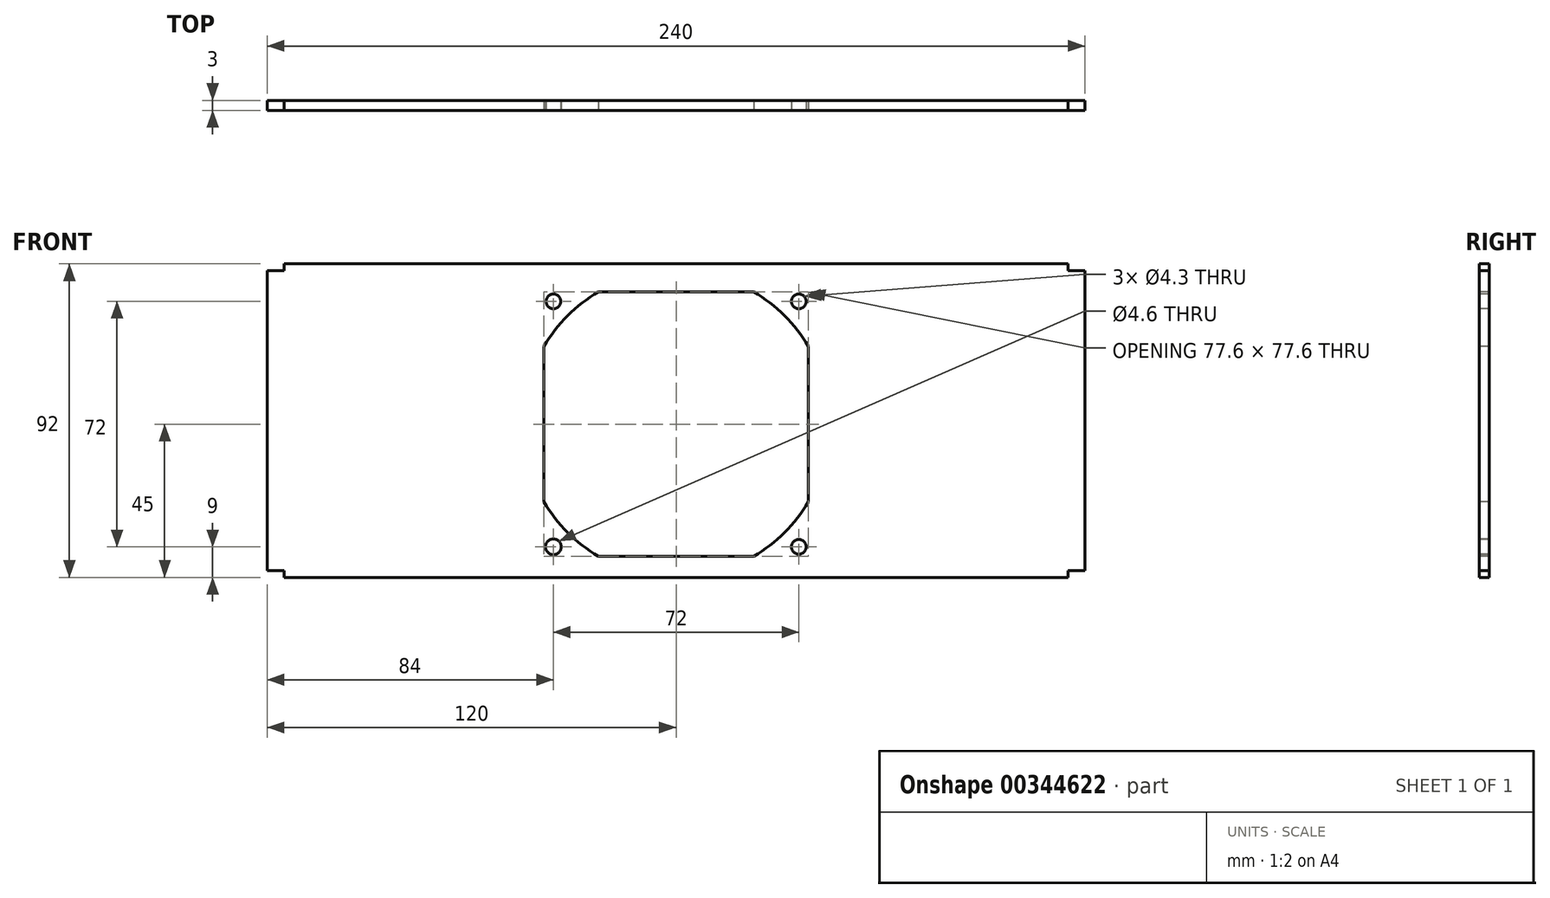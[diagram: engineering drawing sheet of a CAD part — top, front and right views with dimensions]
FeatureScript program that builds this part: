
annotation { "Feature Type Name" : "Feature", "Feature Type Description" : "" }
export const myFeature = defineFeature(function(context is Context, id is Id, definition is map)
    precondition{}
    {
        {
            var Q0;
            Q0=qCreatedBy(makeId("Front.planeOp"),FACE);
            var sketch = newSketch(context, id + "F0", { "sketchPlane" : qUnion([Q0])});
            skLineSegment(sketch, "E0.bottom", {"start": v(120, -47) * mm, "end": v(-120, -47) * mm});
            skLineSegment(sketch, "E0.top", {"start": v(120, 47) * mm, "end": v(-120, 47) * mm});
            skLineSegment(sketch, "E0.left", {"start": v(120, -47) * mm, "end": v(120, 47) * mm});
            skLineSegment(sketch, "E0.right", {"start": v(-120, -47) * mm, "end": v(-120, 47) * mm});
            skPoint(sketch, "E0.middle", {"position": v(0, 0) * mm});
            skSolve(sketch);
        }
        {
            var Q0;
            Q0=qSketchRegion(id+"F0",true);
            extrude(context, id + "F1", {"entities" : qUnion([Q0]), "depth" : 3 * mm});
        }
        {
            var Q0;
            Q0=makeQuery(id+"F1.opExtrude","CAP_FACE",FACE,{"disambiguationData":[OSD([sQuery(id+"F0.wireOp",EDGE,"E0.bottom"),sQuery(id+"F0.wireOp",EDGE,"E0.top"),sQuery(id+"F0.wireOp",EDGE,"E0.left"),sQuery(id+"F0.wireOp",EDGE,"E0.right")])],"isStart":false});
            var sketch = newSketch(context, id + "F2", { "sketchPlane" : qUnion([Q0])});
            skLineSegment(sketch, "E1.bottom", {"start": v(-120, 47) * mm, "end": v(-115, 47) * mm});
            skLineSegment(sketch, "E1.top", {"start": v(-120, 45) * mm, "end": v(-115, 45) * mm});
            skLineSegment(sketch, "E1.left", {"start": v(-120, 47) * mm, "end": v(-120, 45) * mm});
            skLineSegment(sketch, "E1.right", {"start": v(-115, 47) * mm, "end": v(-115, 45) * mm});
            skLineSegment(sketch, "E2.bottom", {"start": v(-120, -47) * mm, "end": v(-115, -47) * mm});
            skLineSegment(sketch, "E2.top", {"start": v(-120, -43) * mm, "end": v(-115, -43) * mm});
            skLineSegment(sketch, "E2.left", {"start": v(-120, -47) * mm, "end": v(-120, -43) * mm});
            skLineSegment(sketch, "E2.right", {"start": v(-115, -47) * mm, "end": v(-115, -43) * mm});
            skLineSegment(sketch, "E3.bottom", {"start": v(120, -47) * mm, "end": v(115, -47) * mm});
            skLineSegment(sketch, "E3.top", {"start": v(120, -43) * mm, "end": v(115, -43) * mm});
            skLineSegment(sketch, "E3.left", {"start": v(120, -47) * mm, "end": v(120, -43) * mm});
            skLineSegment(sketch, "E3.right", {"start": v(115, -47) * mm, "end": v(115, -43) * mm});
            skLineSegment(sketch, "E4.bottom", {"start": v(120, 47) * mm, "end": v(115, 47) * mm});
            skLineSegment(sketch, "E4.top", {"start": v(120, 45) * mm, "end": v(115, 45) * mm});
            skLineSegment(sketch, "E4.left", {"start": v(120, 47) * mm, "end": v(120, 45) * mm});
            skLineSegment(sketch, "E4.right", {"start": v(115, 47) * mm, "end": v(115, 45) * mm});
            skLineSegment(sketch, "E5.bottom", {"start": v(115, -47) * mm, "end": v(-115, -47) * mm});
            skLineSegment(sketch, "E5.top", {"start": v(115, -45) * mm, "end": v(-115, -45) * mm});
            skLineSegment(sketch, "E5.left", {"start": v(115, -47) * mm, "end": v(115, -45) * mm});
            skLineSegment(sketch, "E5.right", {"start": v(-115, -47) * mm, "end": v(-115, -45) * mm});
            skSolve(sketch);
        }
        {
            var Q0;
            Q0=qSketchRegion(id+"F2",true);
            extrude(context, id + "F3", {"entities" : qUnion([Q0]), "operationType" : NewBodyOperationType.REMOVE, "oppositeDirection" : true, "depth" : 25 * mm});
        }
        {
            var Q0;
            Q0=makeQuery(id+"F1.opExtrude","CAP_FACE",FACE,{"disambiguationData":[OSD([sQuery(id+"F0.wireOp",EDGE,"E0.bottom"),sQuery(id+"F0.wireOp",EDGE,"E0.top"),sQuery(id+"F0.wireOp",EDGE,"E0.left"),sQuery(id+"F0.wireOp",EDGE,"E0.right")])],"isStart":false});
            var sketch = newSketch(context, id + "F4", { "sketchPlane" : qUnion([Q0])});
            skLineSegment(sketch, "E6.bottom", {"start": v(40, -40) * mm, "end": v(-40, -40) * mm});
            skLineSegment(sketch, "E6.top", {"start": v(40, 40) * mm, "end": v(-40, 40) * mm});
            skLineSegment(sketch, "E6.left", {"start": v(40, -40) * mm, "end": v(40, 40) * mm});
            skLineSegment(sketch, "E6.right", {"start": v(-40, -40) * mm, "end": v(-40, 40) * mm});
            skPoint(sketch, "E6.middle", {"position": v(0, 0) * mm});
            skLineSegment(sketch, "E7.bottom", {"start": v(36, -36) * mm, "end": v(27, -36) * mm});
            skLineSegment(sketch, "E7.top", {"start": v(36, 36) * mm, "end": v(27, 36) * mm});
            skLineSegment(sketch, "E7.left", {"start": v(36, -36) * mm, "end": v(36, -27) * mm});
            skLineSegment(sketch, "E7.right", {"start": v(-36, -36) * mm, "end": v(-36, -27) * mm});
            skCircle(sketch, "E8", {"center": v(-36, 36) * mm, "radius": 2.15 * mm});
            skCircle(sketch, "E9", {"center": v(36, 36) * mm, "radius": 2.15 * mm});
            skCircle(sketch, "E10", {"center": v(36, -36) * mm, "radius": 2.15 * mm});
            skCircle(sketch, "E11", {"center": v(-36, -36) * mm, "radius": 2.3 * mm});
            skArc(sketch, "E12", {"start": v(22.8, -38.8) * mm, "mid": v(31.82, -31.82) * mm, "end": v(38.8, -22.8) * mm});
            skArc(sketch, "E13.trimOffspring", {"start": v(-38.8, -22.8) * mm, "mid": v(-31.82, -31.82) * mm, "end": v(-22.8, -38.8) * mm});
            skArc(sketch, "E14.trimOffspring", {"start": v(-22.8, 38.8) * mm, "mid": v(-31.82, 31.82) * mm, "end": v(-38.8, 22.8) * mm});
            skArc(sketch, "E15.trimOffspring", {"start": v(38.8, 22.8) * mm, "mid": v(31.82, 31.82) * mm, "end": v(22.8, 38.8) * mm});
            skLineSegment(sketch, "E16.bottom", {"start": v(38.8, -38.8) * mm, "end": v(-38.8, -38.8) * mm});
            skLineSegment(sketch, "E16.top", {"start": v(38.8, 38.8) * mm, "end": v(-38.8, 38.8) * mm});
            skLineSegment(sketch, "E16.left", {"start": v(38.8, -38.8) * mm, "end": v(38.8, 38.8) * mm});
            skLineSegment(sketch, "E16.right", {"start": v(-38.8, -38.8) * mm, "end": v(-38.8, 38.8) * mm});
            skLineSegment(sketch, "E17.trimOffspring", {"start": v(-36, 27) * mm, "end": v(-36, 36) * mm});
            skLineSegment(sketch, "E18.trimOffspring", {"start": v(36, 27) * mm, "end": v(36, 36) * mm});
            skLineSegment(sketch, "E19.trimOffspring", {"start": v(-27, 36) * mm, "end": v(-36, 36) * mm});
            skLineSegment(sketch, "E20.trimOffspring", {"start": v(-27, -36) * mm, "end": v(-36, -36) * mm});
            skSolve(sketch);
        }
        {
            var Q0;
            {var subQ0=sQuery(id+"F4.wireOp",EDGE,"E17.trimOffspring");var subQ1=sQuery(id+"F4.wireOp",EDGE,"E8");var subQ2=makeQuery(id+"F4.imprint","INTERSECT",VERTEX,{"derivedFrom":[subQ1,subQ0]});Q0=makeQuery(id+"F4.imprint","IMPRINT",FACE,{"disambiguationData":[TD([[makeQuery(id+"F4.imprint","IMPRINT",EDGE,{"disambiguationData":[TD([[subQ2,1.0]])],"derivedFrom":subQ1}),1.0]])]});}
            var Q1;
            {var subQ0=sQuery(id+"F4.wireOp",EDGE,"E17.trimOffspring");var subQ1=sQuery(id+"F4.wireOp",EDGE,"E8");var subQ2=makeQuery(id+"F4.imprint","INTERSECT",VERTEX,{"derivedFrom":[subQ1,subQ0]});Q1=makeQuery(id+"F4.imprint","IMPRINT",FACE,{"disambiguationData":[TD([[makeQuery(id+"F4.imprint","IMPRINT",EDGE,{"disambiguationData":[TD([[subQ2,-1.0]])],"derivedFrom":subQ1}),1.0]])]});}
            var Q2;
            {var subQ0=sQuery(id+"F4.wireOp",EDGE,"E18.trimOffspring");var subQ1=sQuery(id+"F4.wireOp",EDGE,"E7.top");var subQ2=makeQuery(id+"F4.imprint","INTERSECT",VERTEX,{"derivedFrom":[subQ1,subQ0]});Q2=makeQuery(id+"F4.imprint","IMPRINT",FACE,{"disambiguationData":[TD([[makeQuery(id+"F4.imprint","IMPRINT",EDGE,{"disambiguationData":[TD([[subQ2,-1.0]])],"derivedFrom":subQ1}),-1.0]])]});}
            var Q3;
            {var subQ0=sQuery(id+"F4.wireOp",EDGE,"E18.trimOffspring");var subQ1=sQuery(id+"F4.wireOp",EDGE,"E7.top");var subQ2=makeQuery(id+"F4.imprint","INTERSECT",VERTEX,{"derivedFrom":[subQ1,subQ0]});Q3=makeQuery(id+"F4.imprint","IMPRINT",FACE,{"disambiguationData":[TD([[makeQuery(id+"F4.imprint","IMPRINT",EDGE,{"disambiguationData":[TD([[subQ2,-1.0]])],"derivedFrom":subQ1}),1.0]])]});}
            var Q4;
            {var subQ0=sQuery(id+"F4.wireOp",EDGE,"E7.left");var subQ1=sQuery(id+"F4.wireOp",EDGE,"E7.bottom");var subQ2=makeQuery(id+"F4.imprint","INTERSECT",VERTEX,{"derivedFrom":[subQ1,subQ0]});Q4=makeQuery(id+"F4.imprint","IMPRINT",FACE,{"disambiguationData":[TD([[makeQuery(id+"F4.imprint","IMPRINT",EDGE,{"disambiguationData":[TD([[subQ2,-1.0]])],"derivedFrom":subQ1}),1.0]])]});}
            var Q5;
            {var subQ0=sQuery(id+"F4.wireOp",EDGE,"E7.left");var subQ1=sQuery(id+"F4.wireOp",EDGE,"E7.bottom");var subQ2=makeQuery(id+"F4.imprint","INTERSECT",VERTEX,{"derivedFrom":[subQ1,subQ0]});Q5=makeQuery(id+"F4.imprint","IMPRINT",FACE,{"disambiguationData":[TD([[makeQuery(id+"F4.imprint","IMPRINT",EDGE,{"disambiguationData":[TD([[subQ2,-1.0]])],"derivedFrom":subQ1}),-1.0]])]});}
            var Q6;
            {var subQ0=sQuery(id+"F4.wireOp",EDGE,"E20.trimOffspring");var subQ1=sQuery(id+"F4.wireOp",EDGE,"E7.right");var subQ2=makeQuery(id+"F4.imprint","INTERSECT",VERTEX,{"derivedFrom":[subQ1,subQ0]});Q6=makeQuery(id+"F4.imprint","IMPRINT",FACE,{"disambiguationData":[TD([[makeQuery(id+"F4.imprint","IMPRINT",EDGE,{"disambiguationData":[TD([[subQ2,-1.0]])],"derivedFrom":subQ1}),1.0]])]});}
            var Q7;
            {var subQ0=sQuery(id+"F4.wireOp",EDGE,"E20.trimOffspring");var subQ1=sQuery(id+"F4.wireOp",EDGE,"E7.right");var subQ2=makeQuery(id+"F4.imprint","INTERSECT",VERTEX,{"derivedFrom":[subQ1,subQ0]});Q7=makeQuery(id+"F4.imprint","IMPRINT",FACE,{"disambiguationData":[TD([[makeQuery(id+"F4.imprint","IMPRINT",EDGE,{"disambiguationData":[TD([[subQ2,-1.0]])],"derivedFrom":subQ1}),-1.0]])]});}
            var Q8;
            {var subQ16=sQuery(id+"F4.wireOp",EDGE,"E12");var subQ17=makeQuery(id+"F4.imprint","INTERSECT",VERTEX,{"derivedFrom":[sQuery(id+"F4.wireOp",EDGE,"E7.bottom"),subQ16]});Q8=makeQuery(id+"F4.imprint","IMPRINT",FACE,{"disambiguationData":[TD([[makeQuery(id+"F4.imprint","IMPRINT",EDGE,{"disambiguationData":[TD([[subQ17,1.0]])],"derivedFrom":subQ16}),1.0]])]});}
            extrude(context, id + "F5", {"entities" : qUnion([Q0, Q1, Q2, Q3, Q4, Q5, Q6, Q7, Q8]), "operationType" : NewBodyOperationType.REMOVE, "oppositeDirection" : true, "depth" : 25 * mm});
        }
    });
